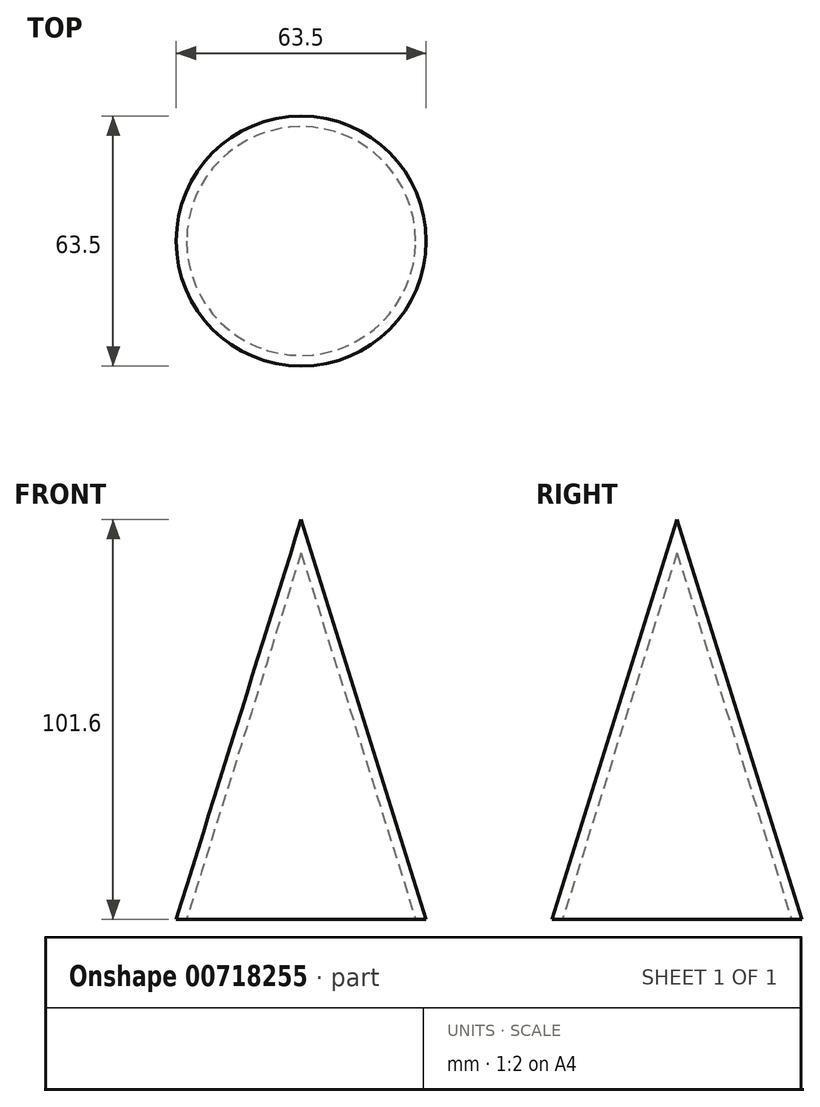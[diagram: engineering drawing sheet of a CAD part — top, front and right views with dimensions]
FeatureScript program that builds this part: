
annotation { "Feature Type Name" : "Feature", "Feature Type Description" : "" }
export const myFeature = defineFeature(function(context is Context, id is Id, definition is map)
    precondition{}
    {
        {
            var Q0;
            Q0=qCreatedBy(makeId("Front.planeOp"),FACE);
            var sketch = newSketch(context, id + "F0", { "sketchPlane" : qUnion([Q0])});
            skLineSegment(sketch, "E0", {"start": v(0, 0) * mm, "end": v(0, 101.6) * mm});
            skLineSegment(sketch, "E1", {"start": v(0, 101.6) * mm, "end": v(31.75, 0) * mm});
            skLineSegment(sketch, "E2", {"start": v(31.75, 0) * mm, "end": v(0, 0) * mm});
            skSolve(sketch);
        }
        {
            var Q0;
            Q0 = qSketchRegion(id + "F0", true);
            var Q1;
            Q1=sQuery(id+"F0.wireOp",EDGE,"E0");
            revolve(context, id + "F1", {"surfaceOperationType" : NewSurfaceOperationType.NEW, "entities" : qUnion([Q0]), "axis" : qUnion([Q1]), "revolveType" : RevolveType.FULL});
        }
        {
            var Q0;
            Q0=makeQuery(id+"F1.opRevolve","SWEPT_FACE",FACE,{"disambiguationData":[OSD([sQuery(id+"F0.wireOp",EDGE,"E2")])]});
            shell(context, id + "F2", {"entities" : qUnion([Q0]), "thickness" : 2.54 * mm});
        }
    });
